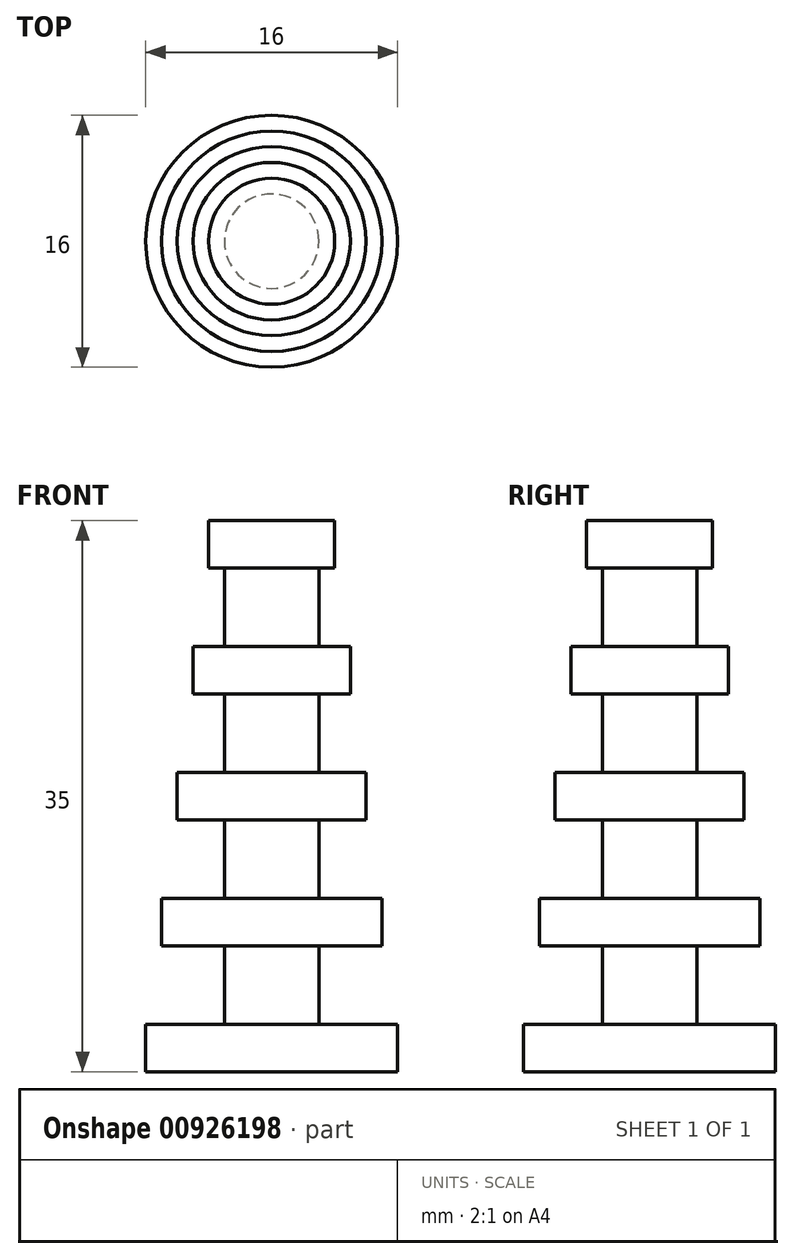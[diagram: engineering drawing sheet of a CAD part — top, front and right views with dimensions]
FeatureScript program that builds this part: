
annotation { "Feature Type Name" : "Feature", "Feature Type Description" : "" }
export const myFeature = defineFeature(function(context is Context, id is Id, definition is map)
    precondition{}
    {
        {
            var Q0;
            Q0=qCreatedBy(makeId("Right.planeOp"),FACE);
            var sketch = newSketch(context, id + "F0", { "sketchPlane" : qUnion([Q0])});
            skLineSegment(sketch, "E0", {"start": v(8, 0) * mm, "end": v(8, 3) * mm});
            skLineSegment(sketch, "E1", {"start": v(8, 3) * mm, "end": v(3, 3) * mm});
            skLineSegment(sketch, "E2", {"start": v(3, 3) * mm, "end": v(3, 8) * mm});
            skLineSegment(sketch, "E3", {"start": v(3, 8) * mm, "end": v(7, 8) * mm});
            skLineSegment(sketch, "E4", {"start": v(7, 8) * mm, "end": v(7, 11) * mm});
            skLineSegment(sketch, "E5", {"start": v(7, 11) * mm, "end": v(3, 11) * mm});
            skLineSegment(sketch, "E6", {"start": v(3, 11) * mm, "end": v(3, 16) * mm});
            skLineSegment(sketch, "E7", {"start": v(3, 16) * mm, "end": v(6, 16) * mm});
            skLineSegment(sketch, "E8", {"start": v(6, 16) * mm, "end": v(6, 19) * mm});
            skLineSegment(sketch, "E9", {"start": v(6, 19) * mm, "end": v(3, 19) * mm});
            skLineSegment(sketch, "E10", {"start": v(3, 19) * mm, "end": v(3, 24) * mm});
            skLineSegment(sketch, "E11", {"start": v(3, 24) * mm, "end": v(5, 24) * mm});
            skLineSegment(sketch, "E12", {"start": v(5, 24) * mm, "end": v(5, 27) * mm});
            skLineSegment(sketch, "E13", {"start": v(5, 27) * mm, "end": v(3, 27) * mm});
            skLineSegment(sketch, "E14", {"start": v(3, 27) * mm, "end": v(3, 32) * mm});
            skLineSegment(sketch, "E15", {"start": v(3, 32) * mm, "end": v(4, 32) * mm});
            skLineSegment(sketch, "E16", {"start": v(4, 32) * mm, "end": v(4, 35) * mm});
            skLineSegment(sketch, "E17", {"start": v(4, 35) * mm, "end": v(0, 35) * mm});
            skLineSegment(sketch, "E18", {"start": v(0, 35) * mm, "end": v(0, 0) * mm});
            skLineSegment(sketch, "E19", {"start": v(8, 0) * mm, "end": v(0, 0) * mm});
            skSolve(sketch);
        }
        {
            var Q0;
            Q0=makeQuery(id+"F0.imprint","IMPRINT",FACE,{"disambiguationData":[TD([[makeQuery(id+"F0.imprint","IMPRINT",EDGE,{"derivedFrom":sQuery(id+"F0.wireOp",EDGE,"E0")}),1.0]])]});
            var Q1;
            Q1=sQuery(id+"F0.wireOp",EDGE,"E18");
            revolve(context, id + "F1", {"surfaceOperationType" : NewSurfaceOperationType.NEW, "entities" : qUnion([Q0]), "axis" : qUnion([Q1]), "revolveType" : RevolveType.FULL});
        }
    });
